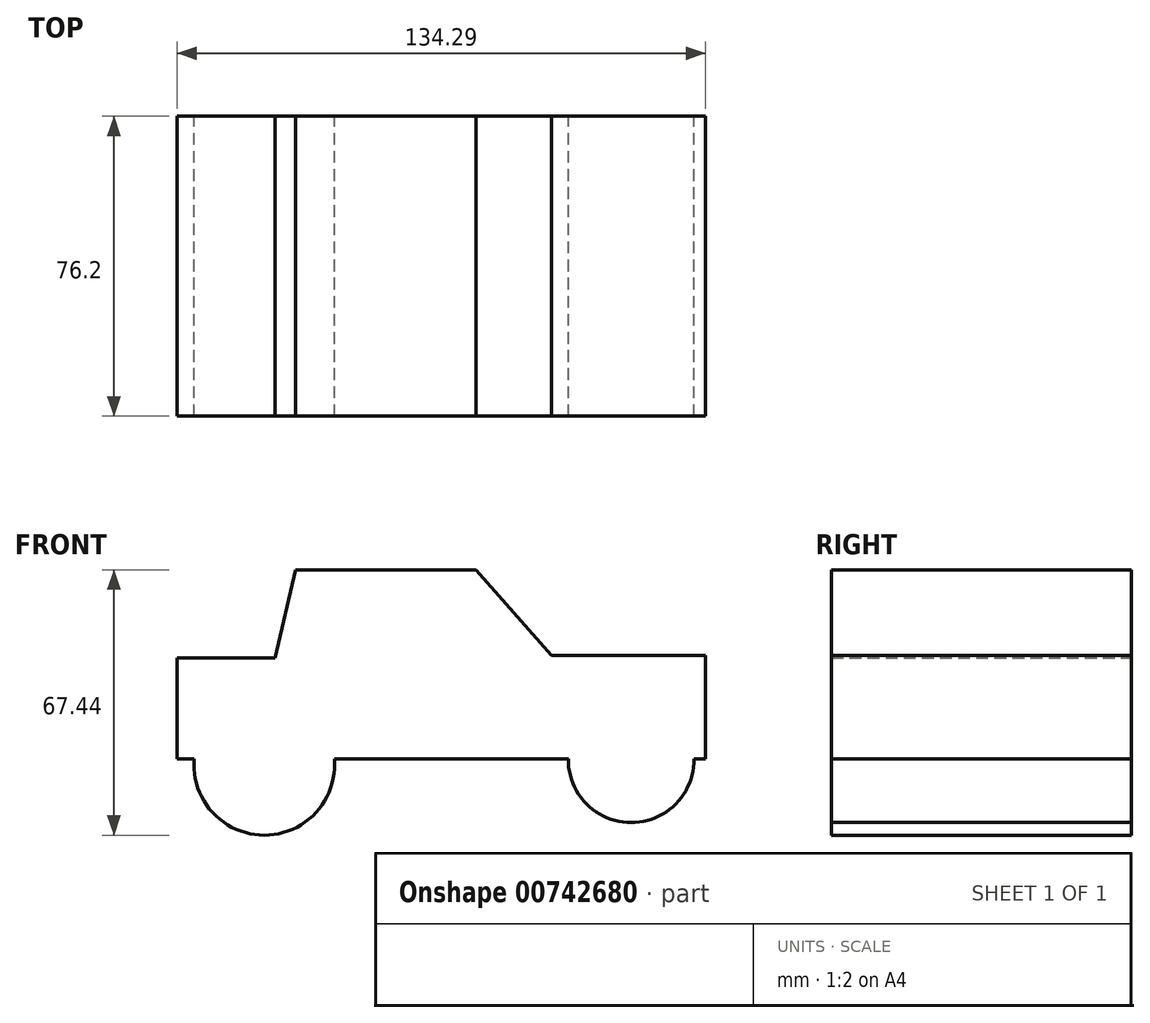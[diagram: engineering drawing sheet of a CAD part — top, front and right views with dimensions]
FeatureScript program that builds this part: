
annotation { "Feature Type Name" : "Feature", "Feature Type Description" : "" }
export const myFeature = defineFeature(function(context is Context, id is Id, definition is map)
    precondition{}
    {
        {
            var Q0;
            Q0=qCreatedBy(makeId("Front.planeOp"),FACE);
            var sketch = newSketch(context, id + "F0", { "sketchPlane" : qUnion([Q0])});
            skLineSegment(sketch, "E0", {"start": v(-60.9, -18.7) * mm, "end": v(58.28, -18.7) * mm});
            skLineSegment(sketch, "E1", {"start": v(58.28, -18.7) * mm, "end": v(58.28, 7.56) * mm});
            skLineSegment(sketch, "E2", {"start": v(58.28, 7.56) * mm, "end": v(19.23, 7.56) * mm});
            skLineSegment(sketch, "E3", {"start": v(19.23, 7.56) * mm, "end": v(0, 29.36) * mm});
            skLineSegment(sketch, "E4", {"start": v(0, 29.36) * mm, "end": v(-45.8, 29.36) * mm});
            skLineSegment(sketch, "E5", {"start": v(-45.8, 29.36) * mm, "end": v(-51, 7) * mm});
            skLineSegment(sketch, "E6", {"start": v(-51, 7) * mm, "end": v(-76, 7) * mm});
            skLineSegment(sketch, "E7", {"start": v(-76, 7) * mm, "end": v(-76, -18.75) * mm});
            skLineSegment(sketch, "E8", {"start": v(-76, -18.75) * mm, "end": v(-53.84, -18.7) * mm});
            skSolve(sketch);
        }
        {
            var Q0;
            {var subQ0=sQuery(id+"F0.wireOp",EDGE,"E1");Q0=makeQuery(id+"F0.imprint","IMPRINT",FACE,{"disambiguationData":[TD([[makeQuery(id+"F0.imprint","IMPRINT",EDGE,{"derivedFrom":subQ0}),1.0]])]});}
            var sketch = newSketch(context, id + "F1", { "sketchPlane" : qUnion([Q0])});
            skSolve(sketch);
        }
        {
            var Q0;
            Q0 = qSketchRegion(id + "F0", true);
            var sketch = newSketch(context, id + "F2", { "sketchPlane" : qUnion([Q0])});
            skCircle(sketch, "E9", {"center": v(39.4, -18.92) * mm, "radius": 15.96 * mm});
            skCircle(sketch, "E10", {"center": v(-53.8, -20.22) * mm, "radius": 17.86 * mm});
            skSolve(sketch);
        }
        {
            var Q0;
            {var subQ1=sQuery(id+"F0.wireOp",EDGE,"E1");var subQ2=makeQuery(id+"F0.imprint","IMPRINT",EDGE,{"derivedFrom":subQ1});Q0=makeQuery(id+"F2.imprint","IMPRINT",FACE,{"disambiguationData":[TD([[makeQuery(id+"F2.imprint","IMPRINT",EDGE,{"derivedFrom":subQ2}),1.0]])]});}
            var Q1;
            {var subQ0=sQuery(id+"F2.wireOp",EDGE,"E10");var subQ2=sQuery(id+"F0.wireOp",EDGE,"E8");var subQ5=makeQuery(id+"F0.imprint","IMPRINT",EDGE,{"derivedFrom":subQ2});var subQ6=makeQuery(id+"F2.imprint","INTERSECT",VERTEX,{"derivedFrom":[subQ5,subQ0]});Q1=makeQuery(id+"F2.imprint","IMPRINT",FACE,{"disambiguationData":[TD([[makeQuery(id+"F2.imprint","IMPRINT",EDGE,{"disambiguationData":[TD([[subQ6,-1.0]])],"derivedFrom":subQ0}),1.0]])]});}
            var Q2;
            {var subQ0=sQuery(id+"F2.wireOp",EDGE,"E10");var subQ2=sQuery(id+"F0.wireOp",EDGE,"E8");var subQ5=makeQuery(id+"F0.imprint","IMPRINT",EDGE,{"derivedFrom":subQ2});var subQ6=makeQuery(id+"F2.imprint","INTERSECT",VERTEX,{"derivedFrom":[subQ5,subQ0]});Q2=makeQuery(id+"F2.imprint","IMPRINT",FACE,{"disambiguationData":[TD([[makeQuery(id+"F2.imprint","IMPRINT",EDGE,{"disambiguationData":[TD([[subQ6,1.0]])],"derivedFrom":subQ0}),1.0]])]});}
            var Q3;
            {var subQ0=sQuery(id+"F2.wireOp",EDGE,"E9");var subQ1=sQuery(id+"F0.wireOp",EDGE,"E0");var subQ2=makeQuery(id+"F0.imprint","IMPRINT",EDGE,{"disambiguationData":[TD([[makeQuery(id+"F0.imprint","INTERSECT",VERTEX,{"derivedFrom":[subQ1,sQuery(id+"F0.wireOp",EDGE,"E1")]}),1.0]])],"derivedFrom":subQ1});var subQ3=makeQuery(id+"F2.imprint","INTERSECT",VERTEX,{"disambiguationData":[OD(0.0)],"derivedFrom":[subQ2,subQ0]});Q3=makeQuery(id+"F2.imprint","IMPRINT",FACE,{"disambiguationData":[TD([[makeQuery(id+"F2.imprint","IMPRINT",EDGE,{"disambiguationData":[TD([[subQ3,1.0]])],"derivedFrom":subQ0}),1.0]])]});}
            var Q4;
            {var subQ0=sQuery(id+"F2.wireOp",EDGE,"E9");var subQ1=sQuery(id+"F0.wireOp",EDGE,"E0");var subQ2=makeQuery(id+"F0.imprint","IMPRINT",EDGE,{"disambiguationData":[TD([[makeQuery(id+"F0.imprint","INTERSECT",VERTEX,{"derivedFrom":[subQ1,sQuery(id+"F0.wireOp",EDGE,"E1")]}),1.0]])],"derivedFrom":subQ1});var subQ3=makeQuery(id+"F2.imprint","INTERSECT",VERTEX,{"disambiguationData":[OD(0.0)],"derivedFrom":[subQ2,subQ0]});Q4=makeQuery(id+"F2.imprint","IMPRINT",FACE,{"disambiguationData":[TD([[makeQuery(id+"F2.imprint","IMPRINT",EDGE,{"disambiguationData":[TD([[subQ3,-1.0]])],"derivedFrom":subQ0}),1.0]])]});}
            extrude(context, id + "F3", {"entities" : qUnion([Q0, Q1, Q2, Q3, Q4]), "depth" : 76.2 * mm, "offsetDistance" : 25.4 * mm});
        }
    });
